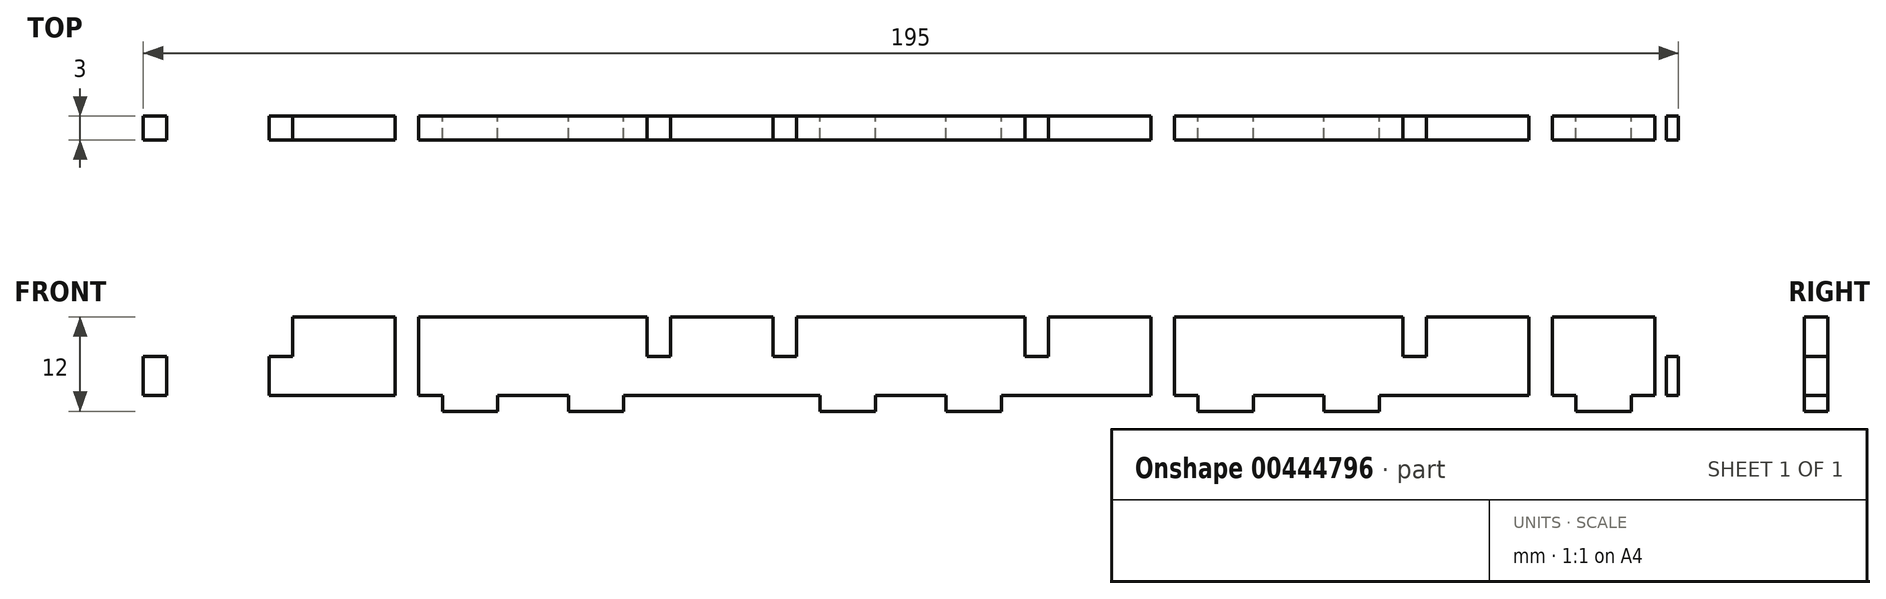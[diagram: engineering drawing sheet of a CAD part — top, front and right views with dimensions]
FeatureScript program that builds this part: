
annotation { "Feature Type Name" : "Feature", "Feature Type Description" : "" }
export const myFeature = defineFeature(function(context is Context, id is Id, definition is map)
    precondition{}
    {
        {
            var Q0;
            Q0=qCreatedBy(makeId("Front.planeOp"),FACE);
            var sketch = newSketch(context, id + "F0", { "sketchPlane" : qUnion([Q0])});
            skLineSegment(sketch, "E0", {"start": v(0, 0) * mm, "end": v(4.5, 0) * mm});
            skLineSegment(sketch, "E1", {"start": v(4.5, 0) * mm, "end": v(4.5, -2) * mm});
            skLineSegment(sketch, "E2", {"start": v(4.5, -2) * mm, "end": v(11.5, -2) * mm});
            skLineSegment(sketch, "E3", {"start": v(11.5, -2) * mm, "end": v(11.5, 0) * mm});
            skLineSegment(sketch, "E4", {"start": v(11.5, 0) * mm, "end": v(36.5, 0) * mm});
            skLineSegment(sketch, "E5", {"start": v(36.5, 0) * mm, "end": v(36.5, -2) * mm});
            skLineSegment(sketch, "E6", {"start": v(36.5, -2) * mm, "end": v(43.5, -2) * mm});
            skLineSegment(sketch, "E7", {"start": v(43.5, -2) * mm, "end": v(43.5, 0) * mm});
            skLineSegment(sketch, "E8", {"start": v(43.5, 0) * mm, "end": v(48, 0) * mm});
            skLineSegment(sketch, "E9.1.0.0", {"start": v(52.5, -2) * mm, "end": v(59.5, -2) * mm});
            skLineSegment(sketch, "E9.1.0.1", {"start": v(59.5, 0) * mm, "end": v(84.5, 0) * mm});
            skLineSegment(sketch, "E9.1.0.2", {"start": v(84.5, -2) * mm, "end": v(91.5, -2) * mm});
            skLineSegment(sketch, "E9.1.0.3", {"start": v(91.5, 0) * mm, "end": v(96, 0) * mm});
            skLineSegment(sketch, "E9.1.0.4", {"start": v(48, 0) * mm, "end": v(52.5, 0) * mm});
            skLineSegment(sketch, "E9.1.0.5", {"start": v(52.5, 0) * mm, "end": v(52.5, -2) * mm});
            skLineSegment(sketch, "E9.1.0.6", {"start": v(91.5, -2) * mm, "end": v(91.5, 0) * mm});
            skLineSegment(sketch, "E9.1.0.7", {"start": v(59.5, -2) * mm, "end": v(59.5, 0) * mm});
            skLineSegment(sketch, "E9.1.0.8", {"start": v(84.5, 0) * mm, "end": v(84.5, -2) * mm});
            skLineSegment(sketch, "E9.2.0.0", {"start": v(100.5, -2) * mm, "end": v(107.5, -2) * mm});
            skLineSegment(sketch, "E9.2.0.1", {"start": v(107.5, 0) * mm, "end": v(132.5, 0) * mm});
            skLineSegment(sketch, "E9.2.0.2", {"start": v(132.5, -2) * mm, "end": v(139.5, -2) * mm});
            skLineSegment(sketch, "E9.2.0.3", {"start": v(139.5, 0) * mm, "end": v(144, 0) * mm});
            skLineSegment(sketch, "E9.2.0.4", {"start": v(96, 0) * mm, "end": v(100.5, 0) * mm});
            skLineSegment(sketch, "E9.2.0.5", {"start": v(100.5, 0) * mm, "end": v(100.5, -2) * mm});
            skLineSegment(sketch, "E9.2.0.6", {"start": v(139.5, -2) * mm, "end": v(139.5, 0) * mm});
            skLineSegment(sketch, "E9.2.0.7", {"start": v(107.5, -2) * mm, "end": v(107.5, 0) * mm});
            skLineSegment(sketch, "E9.2.0.8", {"start": v(132.5, 0) * mm, "end": v(132.5, -2) * mm});
            skLineSegment(sketch, "E9.3.0.0", {"start": v(148.5, -2) * mm, "end": v(155.5, -2) * mm});
            skLineSegment(sketch, "E9.3.0.1", {"start": v(155.5, 0) * mm, "end": v(180.5, 0) * mm});
            skLineSegment(sketch, "E9.3.0.2", {"start": v(180.5, -2) * mm, "end": v(187.5, -2) * mm});
            skLineSegment(sketch, "E9.3.0.3", {"start": v(187.5, 0) * mm, "end": v(192, 0) * mm});
            skLineSegment(sketch, "E9.3.0.4", {"start": v(144, 0) * mm, "end": v(148.5, 0) * mm});
            skLineSegment(sketch, "E9.3.0.5", {"start": v(148.5, 0) * mm, "end": v(148.5, -2) * mm});
            skLineSegment(sketch, "E9.3.0.6", {"start": v(187.5, -2) * mm, "end": v(187.5, 0) * mm});
            skLineSegment(sketch, "E9.3.0.7", {"start": v(155.5, -2) * mm, "end": v(155.5, 0) * mm});
            skLineSegment(sketch, "E9.3.0.8", {"start": v(180.5, 0) * mm, "end": v(180.5, -2) * mm});
            skLineSegment(sketch, "E9.direction1", {"start": v(0, 0) * mm, "end": v(48, 0) * mm, "construction": true});
            skLineSegment(sketch, "E10", {"start": v(0, 0) * mm, "end": v(0, 10) * mm});
            skLineSegment(sketch, "E11", {"start": v(192, 0) * mm, "end": v(192, 10) * mm});
            skLineSegment(sketch, "E12", {"start": v(192, 10) * mm, "end": v(0, 10) * mm});
            skPoint(sketch, "E13.oppositeSnap0", {"position": v(0, 5) * mm});
            skLineSegment(sketch, "E13.bottom", {"start": v(0, 10) * mm, "end": v(-1.5, 10) * mm});
            skLineSegment(sketch, "E13.top", {"start": v(0, 5) * mm, "end": v(-1.5, 5) * mm});
            skLineSegment(sketch, "E13.left", {"start": v(0, 10) * mm, "end": v(0, 5) * mm});
            skLineSegment(sketch, "E13.right", {"start": v(-1.5, 10) * mm, "end": v(-1.5, 5) * mm});
            skPoint(sketch, "E14.oppositeSnap0", {"position": v(192, 5) * mm});
            skLineSegment(sketch, "E14.bottom", {"start": v(192, 10) * mm, "end": v(193.5, 10) * mm});
            skLineSegment(sketch, "E14.top", {"start": v(192, 5) * mm, "end": v(193.5, 5) * mm});
            skLineSegment(sketch, "E14.left", {"start": v(192, 10) * mm, "end": v(192, 5) * mm});
            skLineSegment(sketch, "E14.right", {"start": v(193.5, 10) * mm, "end": v(193.5, 5) * mm});
            skLineSegment(sketch, "E15.bottom", {"start": v(14.5, 10) * mm, "end": v(17.5, 10) * mm});
            skLineSegment(sketch, "E15.top", {"start": v(14.5, 5) * mm, "end": v(17.5, 5) * mm});
            skLineSegment(sketch, "E15.left", {"start": v(14.5, 10) * mm, "end": v(14.5, 5) * mm});
            skLineSegment(sketch, "E15.right", {"start": v(17.5, 10) * mm, "end": v(17.5, 5) * mm});
            skLineSegment(sketch, "E16.bottom", {"start": v(33.5, 10) * mm, "end": v(30.5, 10) * mm});
            skLineSegment(sketch, "E16.top", {"start": v(33.5, 5) * mm, "end": v(30.5, 5) * mm});
            skLineSegment(sketch, "E16.left", {"start": v(33.5, 10) * mm, "end": v(33.5, 5) * mm});
            skLineSegment(sketch, "E16.right", {"start": v(30.5, 10) * mm, "end": v(30.5, 5) * mm});
            skLineSegment(sketch, "E17.bottom", {"start": v(62.5, 10) * mm, "end": v(65.5, 10) * mm});
            skLineSegment(sketch, "E17.top", {"start": v(62.5, 5) * mm, "end": v(65.5, 5) * mm});
            skLineSegment(sketch, "E17.left", {"start": v(62.5, 10) * mm, "end": v(62.5, 5) * mm});
            skLineSegment(sketch, "E17.right", {"start": v(65.5, 10) * mm, "end": v(65.5, 5) * mm});
            skLineSegment(sketch, "E18.bottom", {"start": v(78.5, 10) * mm, "end": v(81.5, 10) * mm});
            skLineSegment(sketch, "E18.top", {"start": v(78.5, 5) * mm, "end": v(81.5, 5) * mm});
            skLineSegment(sketch, "E18.left", {"start": v(78.5, 10) * mm, "end": v(78.5, 5) * mm});
            skLineSegment(sketch, "E18.right", {"start": v(81.5, 10) * mm, "end": v(81.5, 5) * mm});
            skLineSegment(sketch, "E19.bottom", {"start": v(110.5, 10) * mm, "end": v(113.5, 10) * mm});
            skLineSegment(sketch, "E19.top", {"start": v(110.5, 5) * mm, "end": v(113.5, 5) * mm});
            skLineSegment(sketch, "E19.left", {"start": v(110.5, 10) * mm, "end": v(110.5, 5) * mm});
            skLineSegment(sketch, "E19.right", {"start": v(113.5, 10) * mm, "end": v(113.5, 5) * mm});
            skLineSegment(sketch, "E20.bottom", {"start": v(129.5, 10) * mm, "end": v(126.5, 10) * mm});
            skLineSegment(sketch, "E20.top", {"start": v(129.5, 5) * mm, "end": v(126.5, 5) * mm});
            skLineSegment(sketch, "E20.left", {"start": v(129.5, 10) * mm, "end": v(129.5, 5) * mm});
            skLineSegment(sketch, "E20.right", {"start": v(126.5, 10) * mm, "end": v(126.5, 5) * mm});
            skLineSegment(sketch, "E21.bottom", {"start": v(158.5, 10) * mm, "end": v(161.5, 10) * mm});
            skLineSegment(sketch, "E21.top", {"start": v(158.5, 5) * mm, "end": v(161.5, 5) * mm});
            skLineSegment(sketch, "E21.left", {"start": v(158.5, 10) * mm, "end": v(158.5, 5) * mm});
            skLineSegment(sketch, "E21.right", {"start": v(161.5, 10) * mm, "end": v(161.5, 5) * mm});
            skLineSegment(sketch, "E22.bottom", {"start": v(177.5, 10) * mm, "end": v(174.5, 10) * mm});
            skLineSegment(sketch, "E22.top", {"start": v(177.5, 5) * mm, "end": v(174.5, 5) * mm});
            skLineSegment(sketch, "E22.left", {"start": v(177.5, 10) * mm, "end": v(177.5, 5) * mm});
            skLineSegment(sketch, "E22.right", {"start": v(174.5, 10) * mm, "end": v(174.5, 5) * mm});
            skLineSegment(sketch, "E23.top", {"start": v(0, 0) * mm, "end": v(-1.5, 0) * mm});
            skLineSegment(sketch, "E23.left", {"start": v(0, 5) * mm, "end": v(0, 0) * mm});
            skLineSegment(sketch, "E23.right", {"start": v(-1.5, 5) * mm, "end": v(-1.5, 0) * mm});
            skLineSegment(sketch, "E24.top", {"start": v(14.5, 0) * mm, "end": v(17.5, 0) * mm});
            skLineSegment(sketch, "E24.left", {"start": v(14.5, 5) * mm, "end": v(14.5, 0) * mm});
            skLineSegment(sketch, "E24.right", {"start": v(17.5, 5) * mm, "end": v(17.5, 0) * mm});
            skLineSegment(sketch, "E25.bottom", {"start": v(30.5, 5) * mm, "end": v(33.5, 5) * mm});
            skLineSegment(sketch, "E25.top", {"start": v(30.5, 0) * mm, "end": v(33.5, 0) * mm});
            skLineSegment(sketch, "E25.left", {"start": v(30.5, 5) * mm, "end": v(30.5, 0) * mm});
            skLineSegment(sketch, "E25.right", {"start": v(33.5, 5) * mm, "end": v(33.5, 0) * mm});
            skLineSegment(sketch, "E26.top", {"start": v(62.5, 0) * mm, "end": v(65.5, 0) * mm});
            skLineSegment(sketch, "E26.left", {"start": v(62.5, 5) * mm, "end": v(62.5, 0) * mm});
            skLineSegment(sketch, "E26.right", {"start": v(65.5, 5) * mm, "end": v(65.5, 0) * mm});
            skLineSegment(sketch, "E27.top", {"start": v(78.5, 0) * mm, "end": v(81.5, 0) * mm});
            skLineSegment(sketch, "E27.left", {"start": v(78.5, 5) * mm, "end": v(78.5, 0) * mm});
            skLineSegment(sketch, "E27.right", {"start": v(81.5, 5) * mm, "end": v(81.5, 0) * mm});
            skLineSegment(sketch, "E28.top", {"start": v(110.5, 0) * mm, "end": v(113.5, 0) * mm});
            skLineSegment(sketch, "E28.left", {"start": v(110.5, 5) * mm, "end": v(110.5, 0) * mm});
            skLineSegment(sketch, "E28.right", {"start": v(113.5, 5) * mm, "end": v(113.5, 0) * mm});
            skLineSegment(sketch, "E29.bottom", {"start": v(126.5, 5) * mm, "end": v(129.5, 5) * mm});
            skLineSegment(sketch, "E29.top", {"start": v(126.5, 0) * mm, "end": v(129.5, 0) * mm});
            skLineSegment(sketch, "E29.left", {"start": v(126.5, 5) * mm, "end": v(126.5, 0) * mm});
            skLineSegment(sketch, "E29.right", {"start": v(129.5, 5) * mm, "end": v(129.5, 0) * mm});
            skLineSegment(sketch, "E30.top", {"start": v(158.5, 0) * mm, "end": v(161.5, 0) * mm});
            skLineSegment(sketch, "E30.left", {"start": v(158.5, 5) * mm, "end": v(158.5, 0) * mm});
            skLineSegment(sketch, "E30.right", {"start": v(161.5, 5) * mm, "end": v(161.5, 0) * mm});
            skLineSegment(sketch, "E31.bottom", {"start": v(174.5, 5) * mm, "end": v(177.5, 5) * mm});
            skLineSegment(sketch, "E31.top", {"start": v(174.5, 0) * mm, "end": v(177.5, 0) * mm});
            skLineSegment(sketch, "E31.left", {"start": v(174.5, 5) * mm, "end": v(174.5, 0) * mm});
            skLineSegment(sketch, "E31.right", {"start": v(177.5, 5) * mm, "end": v(177.5, 0) * mm});
            skLineSegment(sketch, "E32.top", {"start": v(192, 0) * mm, "end": v(193.5, 0) * mm});
            skLineSegment(sketch, "E32.left", {"start": v(192, 5) * mm, "end": v(192, 0) * mm});
            skLineSegment(sketch, "E32.right", {"start": v(193.5, 5) * mm, "end": v(193.5, 0) * mm});
            skLineSegment(sketch, "E33.bottom", {"start": v(0, 10) * mm, "end": v(1.5, 10) * mm});
            skLineSegment(sketch, "E33.top", {"start": v(0, 5) * mm, "end": v(1.5, 5) * mm});
            skLineSegment(sketch, "E33.right", {"start": v(1.5, 10) * mm, "end": v(1.5, 5) * mm});
            skLineSegment(sketch, "E34.bottom", {"start": v(1.5, 5) * mm, "end": v(0, 5) * mm});
            skLineSegment(sketch, "E34.top", {"start": v(1.5, 0) * mm, "end": v(0, 0) * mm});
            skLineSegment(sketch, "E34.left", {"start": v(1.5, 5) * mm, "end": v(1.5, 0) * mm});
            skLineSegment(sketch, "E35.bottom", {"start": v(192, 10) * mm, "end": v(190.5, 10) * mm});
            skLineSegment(sketch, "E35.top", {"start": v(192, 5) * mm, "end": v(190.5, 5) * mm});
            skLineSegment(sketch, "E35.right", {"start": v(190.5, 10) * mm, "end": v(190.5, 5) * mm});
            skLineSegment(sketch, "E36.bottom", {"start": v(190.5, 5) * mm, "end": v(192, 5) * mm});
            skLineSegment(sketch, "E36.top", {"start": v(190.5, 0) * mm, "end": v(192, 0) * mm});
            skLineSegment(sketch, "E36.left", {"start": v(190.5, 5) * mm, "end": v(190.5, 0) * mm});
            skLineSegment(sketch, "E37.bottom", {"start": v(14.5, 10) * mm, "end": v(11.5, 10) * mm});
            skLineSegment(sketch, "E37.top", {"start": v(14.5, 13) * mm, "end": v(11.5, 13) * mm});
            skLineSegment(sketch, "E37.left", {"start": v(14.5, 10) * mm, "end": v(14.5, 13) * mm});
            skLineSegment(sketch, "E37.right", {"start": v(11.5, 10) * mm, "end": v(11.5, 13) * mm});
            skLineSegment(sketch, "E38.bottom", {"start": v(17.5, 10) * mm, "end": v(20.5, 10) * mm});
            skLineSegment(sketch, "E38.top", {"start": v(17.5, 13) * mm, "end": v(20.5, 13) * mm});
            skLineSegment(sketch, "E38.left", {"start": v(17.5, 10) * mm, "end": v(17.5, 13) * mm});
            skLineSegment(sketch, "E38.right", {"start": v(20.5, 10) * mm, "end": v(20.5, 13) * mm});
            skLineSegment(sketch, "E39.bottom", {"start": v(177.5, 10) * mm, "end": v(180.5, 10) * mm});
            skLineSegment(sketch, "E39.top", {"start": v(177.5, 13) * mm, "end": v(180.5, 13) * mm});
            skLineSegment(sketch, "E39.left", {"start": v(177.5, 10) * mm, "end": v(177.5, 13) * mm});
            skLineSegment(sketch, "E39.right", {"start": v(180.5, 10) * mm, "end": v(180.5, 13) * mm});
            skLineSegment(sketch, "E40.bottom", {"start": v(174.5, 10) * mm, "end": v(171.5, 10) * mm});
            skLineSegment(sketch, "E40.top", {"start": v(174.5, 13) * mm, "end": v(171.5, 13) * mm});
            skLineSegment(sketch, "E40.left", {"start": v(174.5, 10) * mm, "end": v(174.5, 13) * mm});
            skLineSegment(sketch, "E40.right", {"start": v(171.5, 10) * mm, "end": v(171.5, 13) * mm});
            skSolve(sketch);
        }
        {
            var Q0;
            Q0=makeQuery(id+"F0.imprint","IMPRINT",FACE,{"disambiguationData":[TD([[makeQuery(id+"F0.imprint","IMPRINT",EDGE,{"derivedFrom":sQuery(id+"F0.wireOp",EDGE,"E0")}),1.0]])]});
            var Q1;
            Q1=makeQuery(id+"F0.imprint","IMPRINT",FACE,{"disambiguationData":[TD([[makeQuery(id+"F0.imprint","IMPRINT",EDGE,{"derivedFrom":sQuery(id+"F0.wireOp",EDGE,"E15.top")}),-1.0]])]});
            var Q2;
            {var subQ1=sQuery(id+"F0.wireOp",EDGE,"E15.right");Q2=makeQuery(id+"F0.imprint","IMPRINT",FACE,{"disambiguationData":[TD([[makeQuery(id+"F0.imprint","IMPRINT",EDGE,{"derivedFrom":subQ1}),1.0]])]});}
            var Q3;
            Q3=makeQuery(id+"F0.imprint","IMPRINT",FACE,{"disambiguationData":[TD([[makeQuery(id+"F0.imprint","IMPRINT",EDGE,{"derivedFrom":sQuery(id+"F0.wireOp",EDGE,"E25.bottom")}),-1.0]])]});
            var Q4;
            {var subQ4=sQuery(id+"F0.wireOp",EDGE,"E5");Q4=makeQuery(id+"F0.imprint","IMPRINT",FACE,{"disambiguationData":[TD([[makeQuery(id+"F0.imprint","IMPRINT",EDGE,{"derivedFrom":subQ4}),1.0]])]});}
            var Q5;
            Q5=makeQuery(id+"F0.imprint","IMPRINT",FACE,{"disambiguationData":[TD([[makeQuery(id+"F0.imprint","IMPRINT",EDGE,{"derivedFrom":sQuery(id+"F0.wireOp",EDGE,"E17.top")}),-1.0]])]});
            var Q6;
            {var subQ0=sQuery(id+"F0.wireOp",EDGE,"E17.right");Q6=makeQuery(id+"F0.imprint","IMPRINT",FACE,{"disambiguationData":[TD([[makeQuery(id+"F0.imprint","IMPRINT",EDGE,{"derivedFrom":subQ0}),1.0]])]});}
            var Q7;
            Q7=makeQuery(id+"F0.imprint","IMPRINT",FACE,{"disambiguationData":[TD([[makeQuery(id+"F0.imprint","IMPRINT",EDGE,{"derivedFrom":sQuery(id+"F0.wireOp",EDGE,"E18.top")}),-1.0]])]});
            var Q8;
            Q8=makeQuery(id+"F0.imprint","IMPRINT",FACE,{"disambiguationData":[TD([[makeQuery(id+"F0.imprint","IMPRINT",EDGE,{"derivedFrom":sQuery(id+"F0.wireOp",EDGE,"E9.1.0.2")}),1.0]])]});
            var Q9;
            Q9=makeQuery(id+"F0.imprint","IMPRINT",FACE,{"disambiguationData":[TD([[makeQuery(id+"F0.imprint","IMPRINT",EDGE,{"derivedFrom":sQuery(id+"F0.wireOp",EDGE,"E19.top")}),-1.0]])]});
            var Q10;
            {var subQ2=sQuery(id+"F0.wireOp",EDGE,"E19.right");Q10=makeQuery(id+"F0.imprint","IMPRINT",FACE,{"disambiguationData":[TD([[makeQuery(id+"F0.imprint","IMPRINT",EDGE,{"derivedFrom":subQ2}),1.0]])]});}
            var Q11;
            Q11=makeQuery(id+"F0.imprint","IMPRINT",FACE,{"disambiguationData":[TD([[makeQuery(id+"F0.imprint","IMPRINT",EDGE,{"derivedFrom":sQuery(id+"F0.wireOp",EDGE,"E29.bottom")}),-1.0]])]});
            var Q12;
            Q12=makeQuery(id+"F0.imprint","IMPRINT",FACE,{"disambiguationData":[TD([[makeQuery(id+"F0.imprint","IMPRINT",EDGE,{"derivedFrom":sQuery(id+"F0.wireOp",EDGE,"E9.2.0.2")}),1.0]])]});
            var Q13;
            Q13=makeQuery(id+"F0.imprint","IMPRINT",FACE,{"disambiguationData":[TD([[makeQuery(id+"F0.imprint","IMPRINT",EDGE,{"derivedFrom":sQuery(id+"F0.wireOp",EDGE,"E21.top")}),-1.0]])]});
            var Q14;
            {var subQ1=sQuery(id+"F0.wireOp",EDGE,"E21.right");Q14=makeQuery(id+"F0.imprint","IMPRINT",FACE,{"disambiguationData":[TD([[makeQuery(id+"F0.imprint","IMPRINT",EDGE,{"derivedFrom":subQ1}),1.0]])]});}
            var Q15;
            Q15=makeQuery(id+"F0.imprint","IMPRINT",FACE,{"disambiguationData":[TD([[makeQuery(id+"F0.imprint","IMPRINT",EDGE,{"derivedFrom":sQuery(id+"F0.wireOp",EDGE,"E31.bottom")}),-1.0]])]});
            var Q16;
            Q16=makeQuery(id+"F0.imprint","IMPRINT",FACE,{"disambiguationData":[TD([[makeQuery(id+"F0.imprint","IMPRINT",EDGE,{"derivedFrom":sQuery(id+"F0.wireOp",EDGE,"E9.3.0.2")}),1.0]])]});
            var Q17;
            Q17=makeQuery(id+"F0.imprint","IMPRINT",FACE,{"disambiguationData":[TD([[makeQuery(id+"F0.imprint","IMPRINT",EDGE,{"derivedFrom":sQuery(id+"F0.wireOp",EDGE,"E34.bottom")}),1.0]])]});
            var Q18;
            Q18=makeQuery(id+"F0.imprint","IMPRINT",FACE,{"disambiguationData":[TD([[makeQuery(id+"F0.imprint","IMPRINT",EDGE,{"derivedFrom":sQuery(id+"F0.wireOp",EDGE,"E36.bottom")}),-1.0]])]});
            var Q19;
            Q19=makeQuery(id+"F0.imprint","IMPRINT",FACE,{"disambiguationData":[TD([[makeQuery(id+"F0.imprint","IMPRINT",EDGE,{"derivedFrom":sQuery(id+"F0.wireOp",EDGE,"E14.top")}),-1.0]])]});
            var Q20;
            Q20=makeQuery(id+"F0.imprint","IMPRINT",FACE,{"disambiguationData":[TD([[makeQuery(id+"F0.imprint","IMPRINT",EDGE,{"derivedFrom":sQuery(id+"F0.wireOp",EDGE,"E13.top")}),1.0]])]});
            extrude(context, id + "F1", {"entities" : qUnion([Q0, Q1, Q2, Q3, Q4, Q5, Q6, Q7, Q8, Q9, Q10, Q11, Q12, Q13, Q14, Q15, Q16, Q17, Q18, Q19, Q20]), "depth" : 3 * mm});
        }
    });
